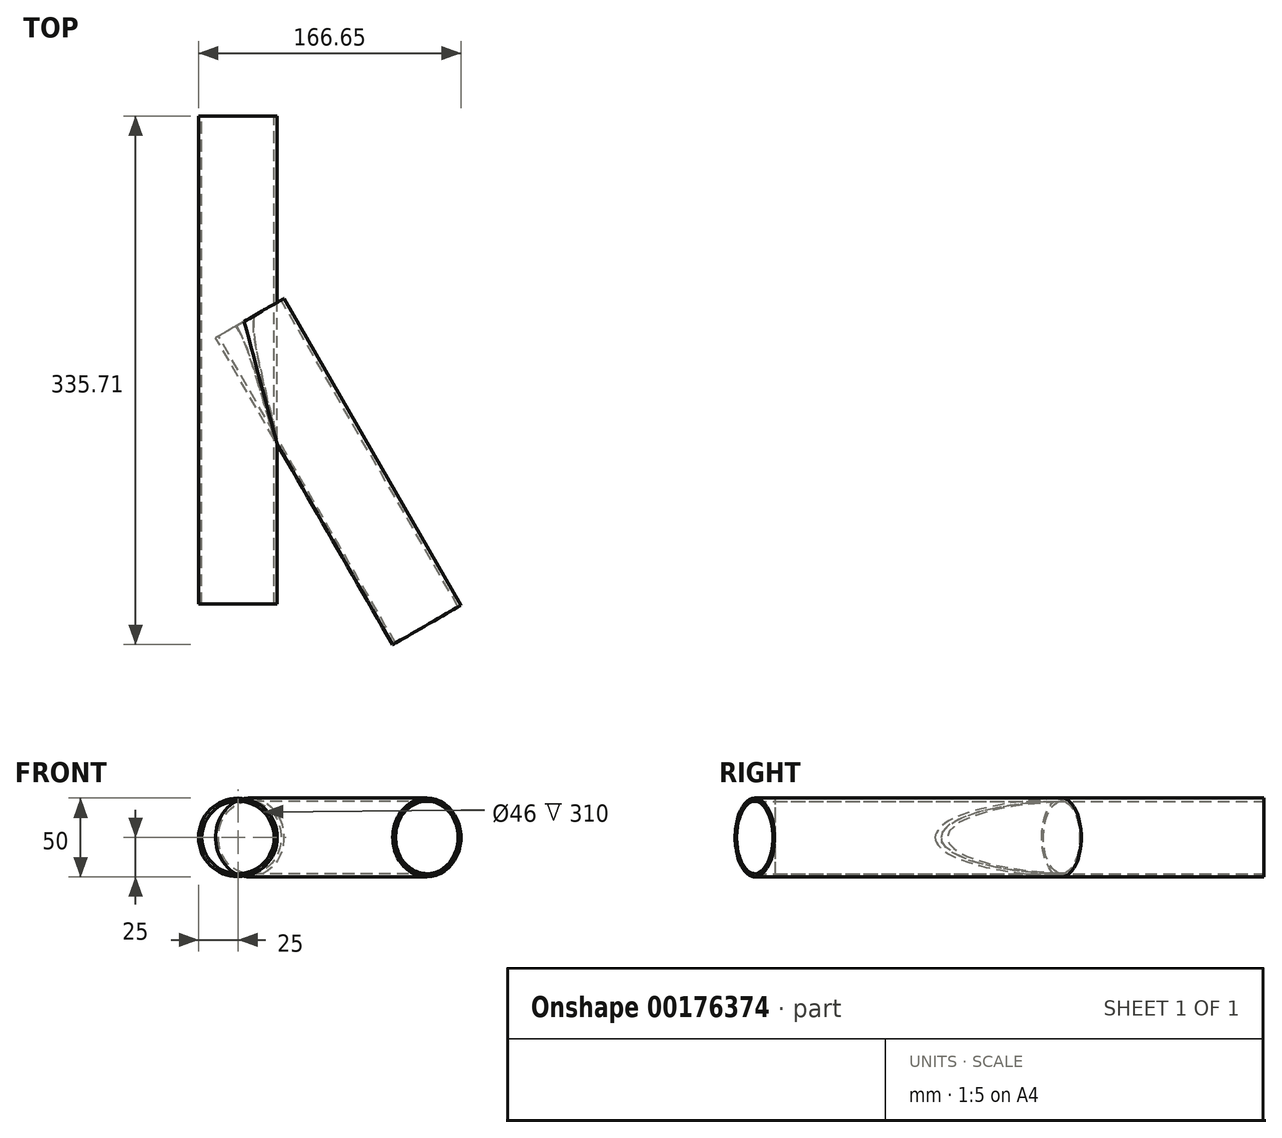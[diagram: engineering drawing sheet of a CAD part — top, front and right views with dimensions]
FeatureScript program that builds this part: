
annotation { "Feature Type Name" : "Feature", "Feature Type Description" : "" }
export const myFeature = defineFeature(function(context is Context, id is Id, definition is map)
    precondition{}
    {
        {
            var Q0;
            Q0=qCreatedBy(makeId("Front.planeOp"),FACE);
            var sketch = newSketch(context, id + "F0", { "sketchPlane" : qUnion([Q0])});
            skCircle(sketch, "E0", {"center": v(0, 0) * mm, "radius": 25 * mm});
            skCircle(sketch, "E1.0", {"center": v(0, 0) * mm, "radius": 23 * mm});
            skSolve(sketch);
        }
        {
            var Q0;
            Q0=makeQuery(id+"F0.imprint","IMPRINT",FACE,{"disambiguationData":[TD([[makeQuery(id+"F0.imprint","IMPRINT",EDGE,{"derivedFrom":sQuery(id+"F0.wireOp",EDGE,"E0")}),1.0]])]});
            extrude(context, id + "F1", {"entities" : qUnion([Q0]), "depth" : 310 * mm});
        }
        {
            var Q0;
            Q0=qCreatedBy(makeId("Right.planeOp"),FACE);
            cPlane(context, id + "F2", {"entities" : qUnion([Q0]), "cplaneType" : CPlaneType.OFFSET, "offset" : 20 * mm, "width" : 150 * mm, "height" : 150 * mm});
        }
        {
            var Q0;
            Q0=qCreatedBy(id+"F2.planeOp",FACE);
            var sketch = newSketch(context, id + "F3", { "sketchPlane" : qUnion([Q0])});
            skLineSegment(sketch, "E2", {"start": v(-310, 25) * mm, "end": v(0, 25) * mm});
            skLineSegment(sketch, "E3", {"start": v(0, -25) * mm, "end": v(-310, -25) * mm});
            skLineSegment(sketch, "E4", {"start": v(-150, 25) * mm, "end": v(-150, -25) * mm});
            skSolve(sketch);
        }
        {
            var Q0;
            Q0=sQuery(id+"F3.wireOp",EDGE,"E4");
            cPlane(context, id + "F4", {"entities" : qUnion([Q0]), "cplaneType" : CPlaneType.LINE_ANGLE, "offset" : 25 * mm, "angle" : 60 * degree, "width" : 150 * mm, "height" : 150 * mm});
        }
        {
            var Q0;
            Q0=qCreatedBy(id+"F4.planeOp",FACE);
            cPlane(context, id + "F5", {"entities" : qUnion([Q0]), "cplaneType" : CPlaneType.OFFSET, "offset" : 200 * mm, "oppositeDirection" : true, "width" : 150 * mm, "height" : 150 * mm});
        }
        {
            var Q0;
            Q0=qCreatedBy(id+"F5.planeOp",FACE);
            var sketch = newSketch(context, id + "F6", { "sketchPlane" : qUnion([Q0])});
            skPoint(sketch, "E5.0", {"position": v(57.68, 0) * mm});
            skCircle(sketch, "E6", {"center": v(57.68, 0) * mm, "radius": 25 * mm});
            skCircle(sketch, "E7.0", {"center": v(57.68, 0) * mm, "radius": 23 * mm});
            skSolve(sketch);
        }
        {
            var Q0;
            Q0=qCreatedBy(id+"F4.planeOp",FACE);
            var sketch = newSketch(context, id + "F7", { "sketchPlane" : qUnion([Q0])});
            skCircle(sketch, "E8.0", {"center": v(57.68, 0) * mm, "radius": 25 * mm});
            skCircle(sketch, "E9.0", {"center": v(57.68, 0) * mm, "radius": 23 * mm});
            skSolve(sketch);
        }
        {
            var Q0;
            Q0=makeQuery(id+"F7.imprint","IMPRINT",FACE,{"disambiguationData":[TD([[makeQuery(id+"F7.imprint","IMPRINT",EDGE,{"derivedFrom":sQuery(id+"F7.wireOp",EDGE,"E8.0")}),1.0]])]});
            var Q1;
            Q1=qCreatedBy(id+"F5.planeOp",FACE);
            extrude(context, id + "F8", {"entities" : qUnion([Q0]), "operationType" : NewBodyOperationType.ADD, "endBound" : BoundingType.UP_TO_SURFACE, "oppositeDirection" : true, "endBoundEntityFace" : qUnion([Q1]), "depth" : 25 * mm, "hasSecondDirection" : true, "secondDirectionOppositeDirection" : false, "secondDirectionDepth" : 25 * mm});
        }
    });
